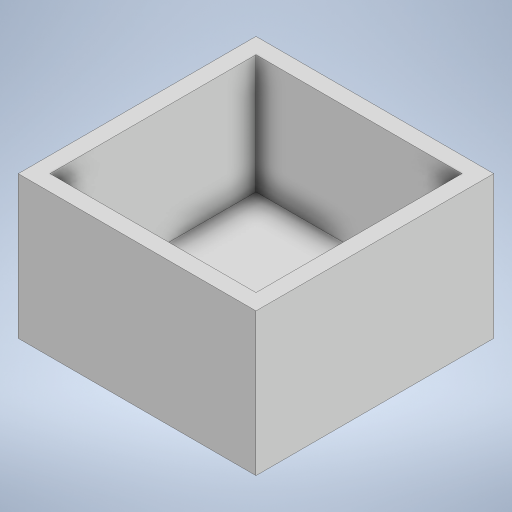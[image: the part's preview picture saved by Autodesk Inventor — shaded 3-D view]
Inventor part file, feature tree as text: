
AUTODESK INVENTOR PART (.ipt)
format: ipt  version: 2023 (Build 270158000, 158)  size: 510,976 bytes
history: native  units: mm
features: extrude x2, sketch x2
ambient origin geometry x8: Origin, YZ Plane, XZ Plane, XY Plane, X Axis, Y Axis, Z Axis, Center Point
bodies: Solid1 (feature_tree)
feature tree (4):
  extrude  "Extrusion1"  Depth=30.0mm
  extrude  "Extrusion2"  Depth=2.0mm
  sketch  "Sketch1"  dims[d0=30.0mm d1=30.0mm]
  sketch  "Sketch2"  dims[d2=2.0mm d3=2.0mm d4=2.0mm d5=2.0mm d6=15.0mm d7=0.0mm d8=3.0mm d9=0.0mm d10=0.5mm d11=0.872665mm]
